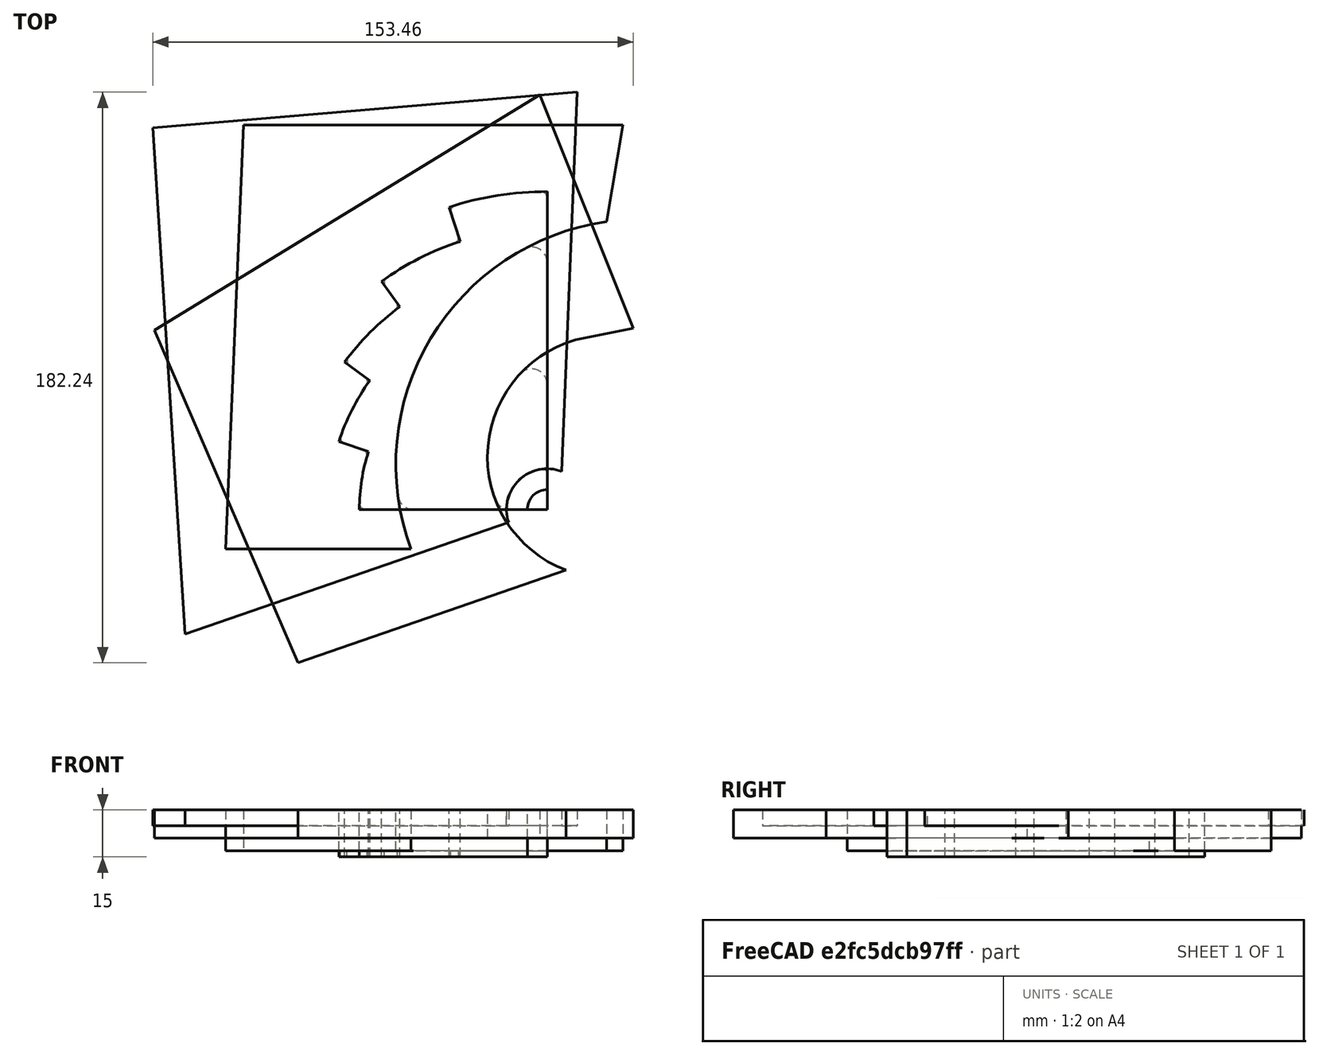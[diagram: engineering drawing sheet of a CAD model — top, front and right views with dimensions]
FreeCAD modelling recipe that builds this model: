
FCSTD DOCUMENT  (FreeCAD 0.16R)
Label: FauxDisque
License: All rights reserved
LicenseURL: http://en.wikipedia.org/wiki/All_rights_reserved
objects: Sketcher::SketchObject×5, PartDesign::Pocket×4, PartDesign::Fillet×3, PartDesign::Pad×1, Mesh::Feature×1
note: 18 computed .brp shape members not serialized (recipe doc carries the construction recipe); baked Part::Feature solids carry a one-line shape summary decoded from their .brp

FEATURE [Sketcher::SketchObject] Sketch
  sketch-geometry (15):
    g0: ArcOfCircle CenterX=0 CenterY=0 CenterZ=0 NormalX=0 NormalY=0 NormalZ=1 Radius=60 StartAngle=2.82743 EndAngle=3.14159
    g1: ArcOfCircle CenterX=0 CenterY=0 CenterZ=0 NormalX=0 NormalY=0 NormalZ=1 Radius=70 StartAngle=2.51327 EndAngle=2.82743
    g2: ArcOfCircle CenterX=0 CenterY=0 CenterZ=0 NormalX=0 NormalY=0 NormalZ=1 Radius=80 StartAngle=2.19911 EndAngle=2.51327
    g3: ArcOfCircle CenterX=0 CenterY=0 CenterZ=0 NormalX=0 NormalY=0 NormalZ=1 Radius=90 StartAngle=1.88496 EndAngle=2.19911
    g4: ArcOfCircle CenterX=0 CenterY=0 CenterZ=0 NormalX=0 NormalY=0 NormalZ=1 Radius=101.5 StartAngle=1.5708 EndAngle=1.88496
    g5: LineSegment StartX=-66.574 StartY=21.6312 StartZ=0 EndX=-57.0634 EndY=18.541 EndZ=0
    g6: LineSegment StartX=-64.7214 StartY=47.0228 StartZ=0 EndX=-56.6312 EndY=41.145 EndZ=0
    g7: LineSegment StartX=-52.9007 StartY=72.8115 StartZ=0 EndX=-47.0228 EndY=64.7214 EndZ=0
    g8: LineSegment StartX=-27.8115 StartY=85.5951 StartZ=0 EndX=-31.3652 EndY=96.5322 EndZ=0
    g9: LineSegment StartX=0 StartY=101.5 StartZ=0 EndX=0 EndY=0 EndZ=0
    g10: LineSegment StartX=-60 StartY=0 StartZ=0 EndX=0 EndY=0 EndZ=0
    g11: LineSegment [constr] StartX=-57.0634 StartY=18.541 StartZ=0 EndX=0 EndY=0 EndZ=0
    g12: LineSegment [constr] StartX=-56.6312 StartY=41.145 StartZ=0 EndX=0 EndY=0 EndZ=0
    g13: LineSegment [constr] StartX=-47.0228 StartY=64.7214 StartZ=0 EndX=0 EndY=0 EndZ=0
    g14: LineSegment [constr] StartX=-27.8115 StartY=85.5951 StartZ=0 EndX=0 EndY=0 EndZ=0
  constraints (40):
    c: Coincident(g0,g-1)
    c: PointOnObject(g0,g-1)
    c: Coincident(g1,g-1)
    c: Coincident(g2,g-1)
    c: Coincident(g4,g-1)
    c: Radius(g0) = 60
    c: Radius(g1) = 70
    c: Radius(g2) = 80
    c: Radius(g3) = 90
    c: Radius(g4) = 101.5
    c: Coincident(g3,g-1)
    c: Coincident(g5,g1)
    c: Coincident(g5,g0)
    c: Coincident(g6,g2)
    c: Coincident(g6,g1)
    c: Coincident(g7,g3)
    c: Coincident(g8,g3)
    c: Coincident(g8,g4)
    c: Coincident(g9,g4)
    c: Coincident(g9,g-1)
    c: Vertical(g9)
    c: Coincident(g10,g0)
    c: Coincident(g10,g-1)
    c: Perpendicular(g0,g5)
    c: Perpendicular(g2,g6)
    c: Perpendicular(g2,g7)
    c: Coincident(g7,g2)
    c: Perpendicular(g3,g8)
    c: Coincident(g11,g0)
    c: Coincident(g11,g-1)
    c: Coincident(g12,g1)
    c: Coincident(g12,g-1)
    c: Coincident(g13,g2)
    c: Coincident(g13,g-1)
    c: Coincident(g14,g3)
    c: Angle(g11) = -0.314159
    c: Angle(g12) = -0.628319
    c: Angle(g13) = -0.942478
    c: Angle(g14) = -1.25664
    c: Coincident(g14,g-1)
FEATURE [PartDesign::Pad] Pad
  Length = 15
  Length2 = 100
  Sketch = -> Sketch
  Type = 0
FEATURE [Sketcher::SketchObject] Sketch001
  Placement = pos=(0,0,15) rot=(0,0,1;0rad)
  Support = -> Pad [Face13]
  sketch-geometry (5):
    g0: LineSegment StartX=-102.652 StartY=-12.6257 StartZ=0 EndX=-43.5134 EndY=-12.6257 EndZ=0
    g1: LineSegment StartX=-102.652 StartY=-12.6257 StartZ=0 EndX=-96.9313 EndY=122.74 EndZ=0
    g2: LineSegment StartX=-96.9313 StartY=122.74 StartZ=0 EndX=24.128 EndY=122.74 EndZ=0
    g3: LineSegment StartX=24.128 StartY=122.74 StartZ=0 EndX=18.8944 EndY=91.8628 EndZ=0
    g4: ArcOfCircle CenterX=29.8292 CenterY=14.4504 CenterZ=0 NormalX=0 NormalY=0 NormalZ=1 Radius=78.1809 StartAngle=1.71112 EndAngle=3.49524
  constraints (7):
    c: Horizontal(g0)
    c: Coincident(g0,g1)
    c: Coincident(g1,g2)
    c: Horizontal(g2)
    c: Coincident(g2,g3)
    c: Coincident(g4,g3)
    c: Coincident(g0,g4)
FEATURE [PartDesign::Pocket] Pocket
  Length = 13
  Sketch = -> Sketch001
  Type = 0
FEATURE [Sketcher::SketchObject] Sketch004
  Placement = pos=(0,0,15) rot=(0,0,1;0rad)
  Support = -> Pocket [Face15]
  sketch-geometry (6):
    g0: ArcOfCircle CenterX=19.6771 CenterY=16.8507 CenterZ=0 NormalX=0 NormalY=0 NormalZ=1 Radius=38.7551 StartAngle=1.76544 EndAngle=4.35005
    g1: LineSegment StartX=12.181 StartY=54.874 StartZ=0 EndX=27.495 EndY=57.8931 EndZ=0
    g2: LineSegment StartX=27.495 StartY=57.8931 StartZ=0 EndX=-2.42502 EndY=132.441 EndZ=0
    g3: LineSegment StartX=-2.42502 StartY=132.441 StartZ=0 EndX=-125.411 EndY=57.2524 EndZ=0
    g4: LineSegment StartX=-125.411 StartY=57.2524 StartZ=0 EndX=-79.5706 EndY=-48.9624 EndZ=0
    g5: LineSegment StartX=-79.5706 StartY=-48.9624 StartZ=0 EndX=5.93978 EndY=-19.388 EndZ=0
  constraints (6):
    c: Tangent(g0,g1) = 1.5708
    c: Coincident(g1,g2)
    c: Coincident(g2,g3)
    c: Coincident(g3,g4)
    c: Coincident(g4,g5)
    c: Coincident(g5,g0)
FEATURE [PartDesign::Pocket] Pocket001
  Length = 9
  Sketch = -> Sketch004
  Type = 0
FEATURE [Sketcher::SketchObject] Sketch005
  Placement = pos=(0,0,15) rot=(0,0,1;0rad)
  Support = -> Pocket001 [Face15]
  sketch-geometry (5):
    g0: ArcOfCircle CenterX=0 CenterY=0 CenterZ=0 NormalX=0 NormalY=0 NormalZ=1 Radius=13 StartAngle=1.20798 EndAngle=3.46243
    g1: LineSegment StartX=4.61376 StartY=12.1537 StartZ=0 EndX=9.594 EndY=133.28 EndZ=0
    g2: LineSegment StartX=9.594 StartY=133.28 StartZ=0 EndX=-125.97 EndY=121.82 EndZ=0
    g3: LineSegment StartX=-125.97 StartY=121.82 StartZ=0 EndX=-115.628 EndY=-39.7385 EndZ=0
    g4: LineSegment StartX=-115.628 StartY=-39.7385 StartZ=0 EndX=-12.3366 EndY=-4.09966 EndZ=0
  constraints (7):
    c: Coincident(g0,g-1)
    c: Coincident(g0,g1)
    c: Coincident(g1,g2)
    c: Coincident(g2,g3)
    c: Coincident(g3,g4)
    c: Coincident(g4,g0)
    c: Radius(g0) = 13
FEATURE [PartDesign::Pocket] Pocket002
  Length = 5
  Sketch = -> Sketch005
  Type = 0
FEATURE [Sketcher::SketchObject] Sketch003
  Placement = pos=(0,0,15) rot=(0,0,1;0rad)
  Support = -> Pocket002 [Face15]
  sketch-geometry (1):
    g0: Circle CenterX=0 CenterY=0 CenterZ=0 NormalX=0 NormalY=0 NormalZ=1 Radius=6.35
  constraints (2):
    c: Coincident(g0,g-1)
    c: Radius(g0) = 6.35
FEATURE [PartDesign::Pocket] Pocket003
  Length = 5
  Sketch = -> Sketch003
  Type = 1
FEATURE [PartDesign::Fillet] Fillet
  Base = -> Pocket003 [Edge45,Edge47,Edge46,Edge48,Edge49,Edge16,Edge2,Edge4,Edge28,Edge29]
  Radius = 2
FEATURE [PartDesign::Fillet] Fillet001
  Base = -> Fillet [Edge67,Edge71,Edge56,Edge60]
  Radius = 5
FEATURE [PartDesign::Fillet] Fillet002
  Base = -> Fillet001 [Edge39]
  Radius = 1
FEATURE [Mesh::Feature] Mesh  label="Fillet002 (Meshed)"
